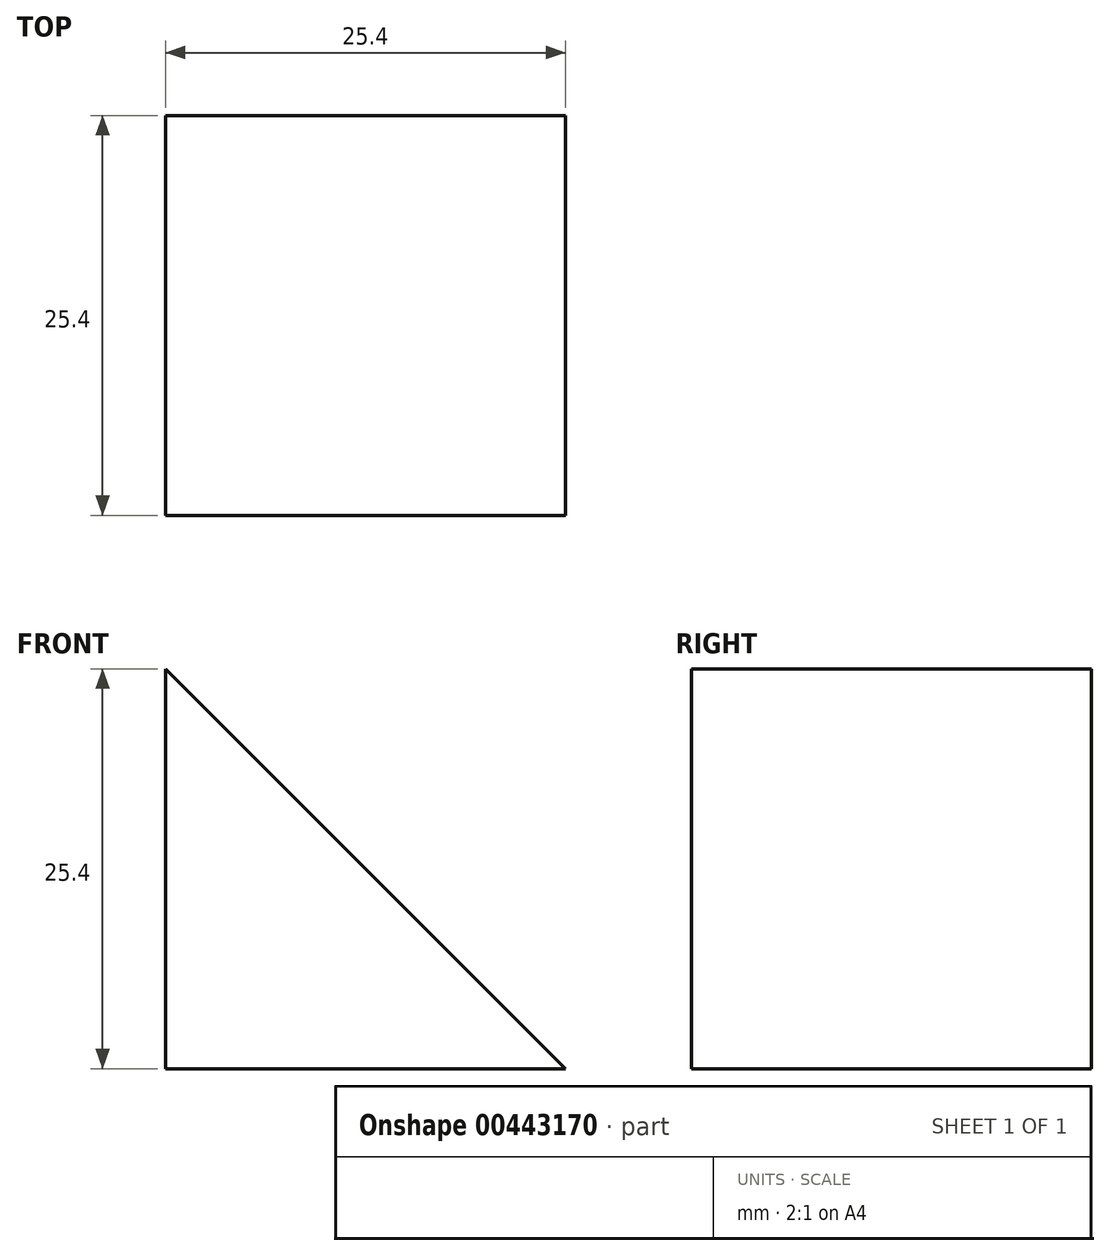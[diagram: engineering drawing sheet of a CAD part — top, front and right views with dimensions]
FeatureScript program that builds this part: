
annotation { "Feature Type Name" : "Feature", "Feature Type Description" : "" }
export const myFeature = defineFeature(function(context is Context, id is Id, definition is map)
    precondition{}
    {
        {
            var Q0;
            Q0=qCreatedBy(makeId("Front.planeOp"),FACE);
            var sketch = newSketch(context, id + "F0", { "sketchPlane" : qUnion([Q0])});
            skLineSegment(sketch, "E0", {"start": v(-45.9, 25.4) * mm, "end": v(-45.9, 0) * mm});
            skLineSegment(sketch, "E1", {"start": v(-45.9, 0) * mm, "end": v(-20.5, 0) * mm});
            skLineSegment(sketch, "E2", {"start": v(-45.9, 25.4) * mm, "end": v(-20.5, 0) * mm});
            skSolve(sketch);
        }
        {
            var Q0;
            Q0=makeQuery(id+"F0.imprint","IMPRINT",FACE,{"disambiguationData":[TD([[makeQuery(id+"F0.imprint","IMPRINT",EDGE,{"derivedFrom":sQuery(id+"F0.wireOp",EDGE,"E0")}),1.0]])]});
            extrude(context, id + "F1", {"entities" : qUnion([Q0]), "depth" : 25.4 * mm});
        }
    });
